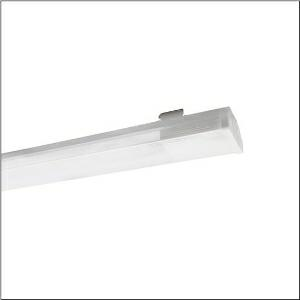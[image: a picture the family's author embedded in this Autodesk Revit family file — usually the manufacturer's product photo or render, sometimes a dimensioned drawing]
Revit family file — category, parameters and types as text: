
# Revit family: modario_31_gen_2_53bm812du4gxc23s_f5aa
name_source: partatom
category: Lighting Fixtures
units: mm (PartAtom-declared; Revit-internal decimal feet)

## family parameters
Cut with Voids When Loaded = No
Host = Face
Light Source = No
Part Type = Normal
Room Calculation Point = No
Round Connector Dimension = Use Diameter
Shared = No

## types (1)
- --- (1 x LED, 950 lm, 6.8 W, 4000K)
    Apparent Load = 7 VA
    CIE Flux Codes = 47 80 95 93 100
    Color Rendering = 80
    Color Temperature = 4000K
    Default Elevation = 1800 mm
    Description = Modario 31 Gen.2, luminaire insert, of sheet steel, coil coated, white, length: 2.392mm, width: 81mm, height: 82mm, 8x system unit, system units: 299mm, LED rated luminous flux: 16.290lm, light colour: 840, SDCM (Standard Deviation of Colour Matching)MacAdam ≤ 3 SDCM (initial), control gear: DALI 2, with plug, 6-pole, with phase selection, mains connection: 220..240V, AC, 50/60Hz, rated input power: 96W, for emergency light function, through-wiring accessed according to module size, converter,control gear: single battery element, battery: LiFePO4, 9Ah, primary optical cover: cover, of PMMA, light emission: direct distribution, primary light characteristic: symmetric, protection rating (complete): IP20, protection rating (LED compartment): IP50, insulation class (complete): insulation class I (protective earthing), certification: CE, UKCA, impact resistance: IK03, permissible ambient temperature for indoor applications: +5..+40°C, standard: EN 60598-2-22, corresponds to IFS (International Featured Standards) requirements for safety and quality in the food industry, reducing of maximum allowable ambient temperature of 5°C with ceiling mounting, IP40 when using the optional accessory 5TP9018, packaging unit: 1 piece
    Height = 92 mm
    Lamp = 1 x LED
    Lamp Light Flux = 950 lm
    Lamp Power = 6.8 W
    Lamp count = 1
    Length = 2392 mm
    Luminous efficacy = 140 lm/W
    Manufacturer = Siteco
    ModVariant = No
    Model = 53BM812DU4GXC23S
    Mounting Place = Ceiling
    Mounting Type = Pendant
    Number of Poles = 1
    OnlyDefault = Yes
    Power Factor = 1
    Product Name = Modario 31 Gen.2
    Product group = luminaire insert | ceiling pendant
    ProductGroupID = 901
    Protection Class = Protection class I
    Protection Degree = IP 20
    RLX_Detail_Level = 1
    RLX_Emergency_Light_Flux = 0 lm
    RLX_Emergency_Type = 0
    RLX_Emergency_Type_DB = No
    RlxData = <blob elided: 38453 chars, md5=9476f71f>
    Socket = socket
    Standby Power = 0 W
    System Light Flux = 950 lm
    System Power = 7 W
    Type Comments = : emergency light operation: 3 h
    Type Image = l_1341883.jpg
    URL = http://relux.com
    VarID = @adj_050435
    Voltage = 0 V
    Weight = 0.00 kg
    Width = 81 mm

## geometry (parser evidence)
native form markers: Blend x4, Sweep x13
no freeform markers — native parametric forms only
